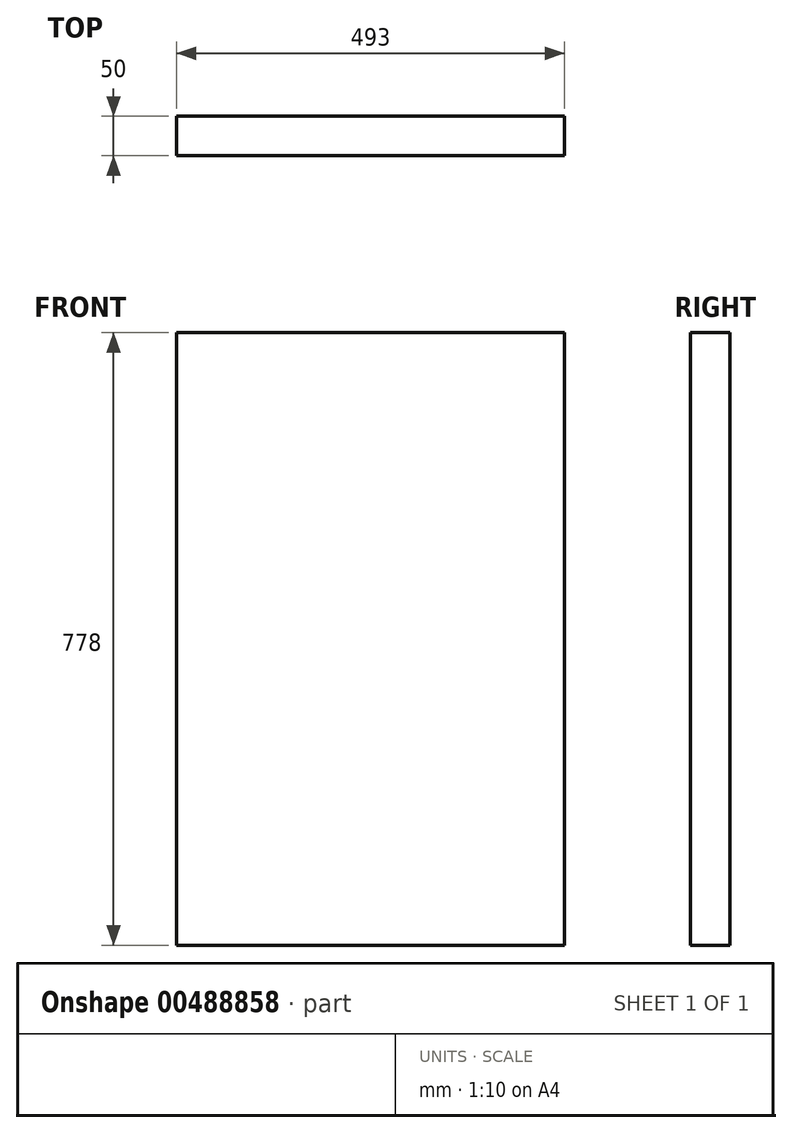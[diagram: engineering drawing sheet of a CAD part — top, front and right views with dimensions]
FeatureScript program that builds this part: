
annotation { "Feature Type Name" : "Feature", "Feature Type Description" : "" }
export const myFeature = defineFeature(function(context is Context, id is Id, definition is map)
    precondition{}
    {
        {
            var Q0;
            Q0=qCreatedBy(makeId("Front.planeOp"),FACE);
            var sketch = newSketch(context, id + "F0", { "sketchPlane" : qUnion([Q0])});
            skLineSegment(sketch, "E0.bottom", {"start": v(-246.5, 389) * mm, "end": v(246.5, 389) * mm});
            skLineSegment(sketch, "E0.top", {"start": v(-246.5, -389) * mm, "end": v(246.5, -389) * mm});
            skLineSegment(sketch, "E0.left", {"start": v(-246.5, 389) * mm, "end": v(-246.5, -389) * mm});
            skLineSegment(sketch, "E0.right", {"start": v(246.5, 389) * mm, "end": v(246.5, -389) * mm});
            skPoint(sketch, "E0.middle", {"position": v(0, 0) * mm});
            skSolve(sketch);
        }
        {
            var Q0;
            Q0 = qSketchRegion(id + "F0", true);
            extrude(context, id + "F1", {"entities" : qUnion([Q0]), "depth" : 50 * mm});
        }
    });
